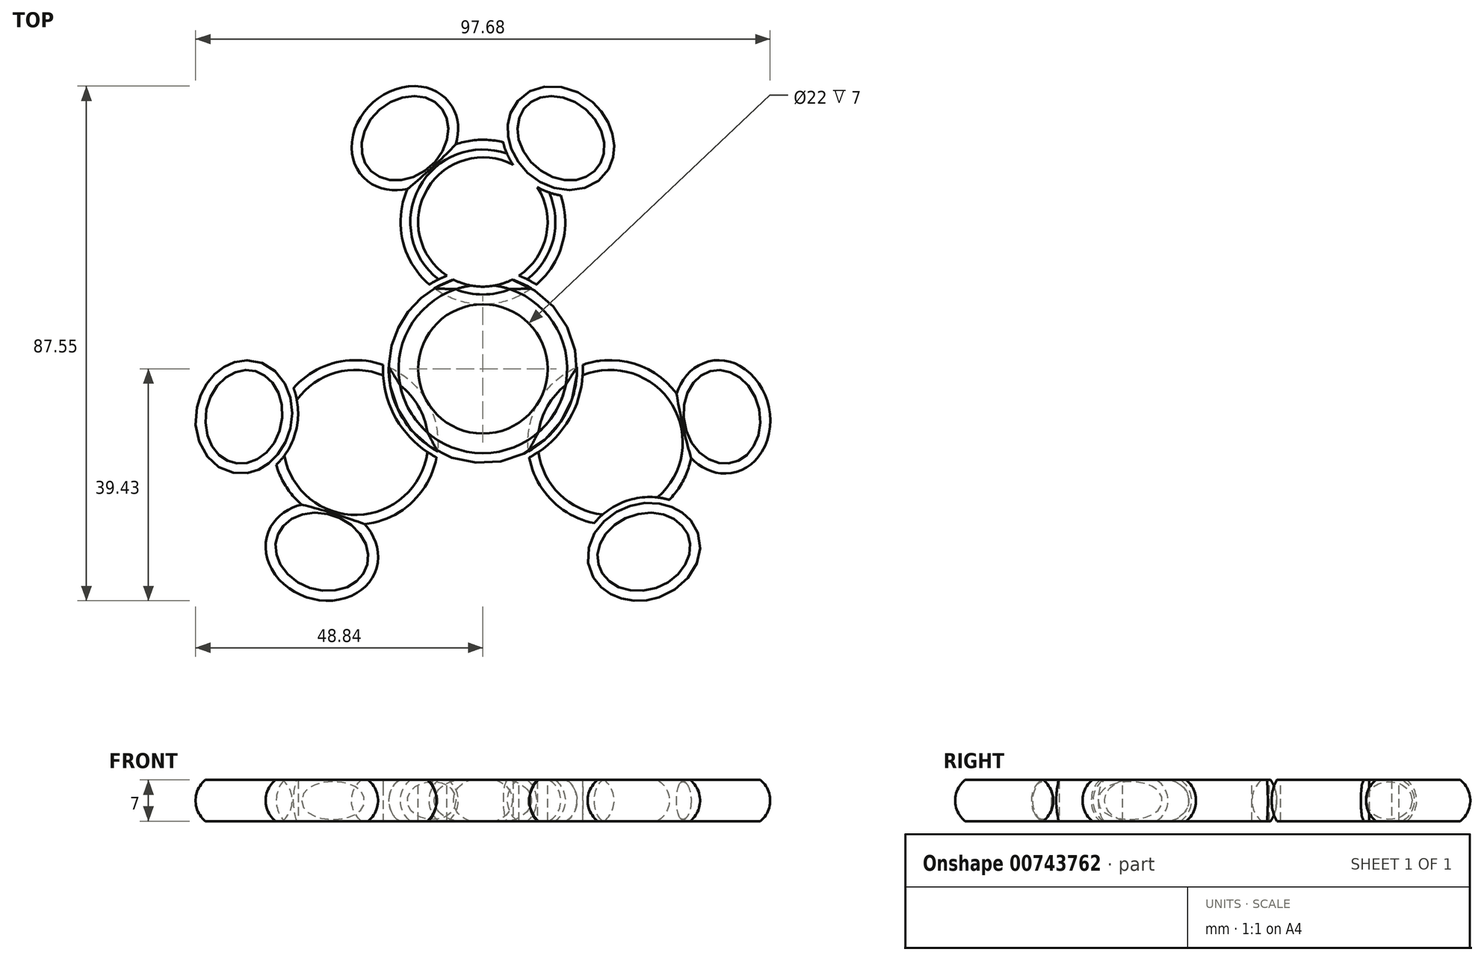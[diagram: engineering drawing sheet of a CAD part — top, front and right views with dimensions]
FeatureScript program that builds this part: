
annotation { "Feature Type Name" : "Feature", "Feature Type Description" : "" }
export const myFeature = defineFeature(function(context is Context, id is Id, definition is map)
    precondition{}
    {
        {
            var Q0;
            Q0=qCreatedBy(makeId("Front.planeOp"),FACE);
            var sketch = newSketch(context, id + "F0", { "sketchPlane" : qUnion([Q0])});
            skLineSegment(sketch, "E0", {"start": v(0, 15.15) * mm, "end": v(0, -20.96) * mm, "construction": true});
            skSolve(sketch);
        }
        {
            var Q0;
            Q0=qCreatedBy(makeId("Top.planeOp"),FACE);
            var sketch = newSketch(context, id + "F1", { "sketchPlane" : qUnion([Q0])});
            skCircle(sketch, "E1", {"center": v(0, 0) * mm, "radius": 39 * mm});
            skCircle(sketch, "E2", {"center": v(0, 0) * mm, "radius": 25 * mm});
            skCircle(sketch, "E3", {"center": v(0, 25) * mm, "radius": 11 * mm});
            skCircle(sketch, "E4", {"center": v(0, 0) * mm, "radius": 11 * mm});
            skCircle(sketch, "E5", {"center": v(0, -25) * mm, "radius": 11 * mm});
            skSolve(sketch);
        }
        {
            var Q0;
            Q0=qCreatedBy(makeId("Top.planeOp"),FACE);
            var sketch = newSketch(context, id + "F2", { "sketchPlane" : qUnion([Q0])});
            skCircle(sketch, "E6", {"center": v(0, 25) * mm, "radius": 14 * mm});
            skSolve(sketch);
        }
        {
            var Q0;
            Q0=qCreatedBy(makeId("Top.planeOp"),FACE);
            var sketch = newSketch(context, id + "F3", { "sketchPlane" : qUnion([Q0])});
            skEllipse(sketch, "E7.MirrorC", {"center": v(13.26, 39.26) * mm, "majorRadius": 9.7 * mm, "minorRadius": 8.15 * mm, "majorAxis": v(-0.75, 0.66)});
            skLineSegment(sketch, "E8", {"start": v(5.97, 45.67) * mm, "end": v(20.54, 32.85) * mm, "construction": true});
            skSolve(sketch);
        }
        {
            var Q0;
            Q0=qSketchRegion(id+"F2",true);
            extrude(context, id + "F4", {"entities" : qUnion([Q0]), "endBound" : BoundingType.SYMMETRIC, "depth" : 7 * mm, "offsetDistance" : 25 * mm});
        }
        {
            var Q0;
            Q0=qCreatedBy(makeId("Right.planeOp"),FACE);
            var sketch = newSketch(context, id + "F5", { "sketchPlane" : qUnion([Q0])});
            skLineSegment(sketch, "E9", {"start": v(39, 3.5) * mm, "end": v(39, -3.5) * mm, "construction": true});
            skArc(sketch, "E10", {"start": v(37.33, -3.5) * mm, "mid": v(39, 0) * mm, "end": v(37.33, 3.5) * mm});
            skLineSegment(sketch, "E11", {"start": v(37.33, 3.5) * mm, "end": v(40, 3.5) * mm});
            skLineSegment(sketch, "E12", {"start": v(40, 3.5) * mm, "end": v(40, -3.5) * mm});
            skLineSegment(sketch, "E13", {"start": v(40, -3.5) * mm, "end": v(37.33, -3.5) * mm});
            skSolve(sketch);
        }
        {
            var Q0;
            Q0=makeQuery(id+"F5.imprint","IMPRINT",FACE,{"disambiguationData":[TD([[makeQuery(id+"F5.imprint","IMPRINT",EDGE,{"derivedFrom":sQuery(id+"F5.wireOp",EDGE,"E10")}),-1.0]])]});
            var Q1;
            Q1=makeQuery(id+"F4.opExtrude","CAP_EDGE",EDGE,{"disambiguationData":[OSD([sQuery(id+"F2.wireOp",EDGE,"E6")])],"isStart":false});
            sweep(context, id + "F6", {"operationType" : NewBodyOperationType.REMOVE, "profiles" : qUnion([Q0]), "path" : qUnion([Q1])});
        }
        {
            var Q0;
            Q0=qSketchRegion(id+"F3",true);
            var Q1;
            Q1=makeQuery(id+"F4.opExtrude","CAP_FACE",FACE,{"disambiguationData":[OSD([sQuery(id+"F2.wireOp",EDGE,"E6")])],"isStart":false});
            var Q2;
            Q2=makeQuery(id+"F4.opExtrude","CAP_FACE",FACE,{"disambiguationData":[OSD([sQuery(id+"F2.wireOp",EDGE,"E6")])],"isStart":true});
            extrude(context, id + "F7", {"entities" : qUnion([Q0]), "endBound" : BoundingType.UP_TO_SURFACE, "depth" : 25 * mm, "endBoundEntityFace" : qUnion([Q1]), "offsetDistance" : 25 * mm, "hasSecondDirection" : true, "secondDirectionBound" : SecondDirectionBoundingType.UP_TO_SURFACE, "secondDirectionOppositeDirection" : true, "secondDirectionDepth" : 25 * mm, "secondDirectionBoundEntityFace" : qUnion([Q2])});
        }
        {
            var Q0;
            Q0=sQuery(id+"F3.wireOp",EDGE,"E8");
            cPoint(context, id + "F8", {"entities" : qUnion([Q0]), "parameter" : 0.5});
        }
        {
            var Q0;
            Q0=qCreatedBy(id+"F8",VERTEX);
            var Q1;
            Q1=sQuery(id+"F3.wireOp",EDGE,"E8");
            cPlane(context, id + "F9", {"entities" : qUnion([Q0, Q1]), "cplaneType" : CPlaneType.LINE_POINT, "offset" : 25 * mm, "width" : 150 * mm, "height" : 150 * mm});
        }
        {
            var Q0;
            Q0=qCreatedBy(id+"F9.planeOp",FACE);
            var sketch = newSketch(context, id + "F10", { "sketchPlane" : qUnion([Q0])});
            skArc(sketch, "E14", {"start": v(44.71, -3.5) * mm, "mid": v(46.39, 0) * mm, "end": v(44.71, 3.5) * mm});
            skLineSegment(sketch, "E15", {"start": v(46.39, 3.5) * mm, "end": v(46.39, -3.5) * mm, "construction": true});
            skLineSegment(sketch, "E16", {"start": v(44.71, 3.5) * mm, "end": v(47.39, 3.5) * mm});
            skLineSegment(sketch, "E17", {"start": v(47.39, 3.5) * mm, "end": v(47.39, -3.5) * mm});
            skLineSegment(sketch, "E18", {"start": v(47.39, -3.5) * mm, "end": v(44.71, -3.5) * mm});
            skSolve(sketch);
        }
        {
            var Q0;
            Q0=makeQuery(id+"F10.imprint","IMPRINT",FACE,{"disambiguationData":[TD([[makeQuery(id+"F10.imprint","IMPRINT",EDGE,{"derivedFrom":sQuery(id+"F10.wireOp",EDGE,"E14")}),-1.0]])]});
            var Q1;
            Q1=makeQuery(id+"F7.opExtrude","CAP_EDGE",EDGE,{"disambiguationData":[OSD([sQuery(id+"F3.wireOp",EDGE,"E7.MirrorC")])],"isStart":false});
            sweep(context, id + "F11", {"operationType" : NewBodyOperationType.REMOVE, "profiles" : qUnion([Q0]), "path" : qUnion([Q1])});
        }
        {
            var Q0;
            Q0=makeQuery(id+"F7.opExtrude","SWEPT_BODY",BODY,{"disambiguationData":[OSD([sQuery(id+"F3.wireOp",EDGE,"E7.MirrorC")])]});
            var Q1;
            Q1=qCreatedBy(makeId("Right.planeOp"),FACE);
            mirror(context, id + "F12", {"operationType" : NewBodyOperationType.ADD, "entities" : qUnion([Q0]), "mirrorPlane" : qUnion([Q1])});
        }
        {
            var Q0;
            Q0=qCreatedBy(makeId("Top.planeOp"),FACE);
            var sketch = newSketch(context, id + "F13", { "sketchPlane" : qUnion([Q0])});
            skCircle(sketch, "E19", {"center": v(0, 0) * mm, "radius": 16 * mm});
            skSolve(sketch);
        }
        {
            var Q0;
            Q0=qSketchRegion(id+"F13",true);
            var Q1;
            Q1=makeQuery(id+"F4.opExtrude","CAP_FACE",FACE,{"disambiguationData":[OSD([sQuery(id+"F2.wireOp",EDGE,"E6")])],"isStart":false});
            var Q2;
            Q2=makeQuery(id+"F4.opExtrude","CAP_FACE",FACE,{"disambiguationData":[OSD([sQuery(id+"F2.wireOp",EDGE,"E6")])],"isStart":true});
            extrude(context, id + "F14", {"entities" : qUnion([Q0]), "endBound" : BoundingType.UP_TO_SURFACE, "depth" : 25 * mm, "endBoundEntityFace" : qUnion([Q1]), "offsetDistance" : 25 * mm, "hasSecondDirection" : true, "secondDirectionBound" : SecondDirectionBoundingType.UP_TO_SURFACE, "secondDirectionOppositeDirection" : true, "secondDirectionDepth" : 25 * mm, "secondDirectionBoundEntityFace" : qUnion([Q2])});
        }
        {
            var Q0;
            Q0=qCreatedBy(makeId("Right.planeOp"),FACE);
            var sketch = newSketch(context, id + "F15", { "sketchPlane" : qUnion([Q0])});
            skArc(sketch, "E20", {"start": v(14.33, -3.5) * mm, "mid": v(16, 0) * mm, "end": v(14.33, 3.5) * mm});
            skLineSegment(sketch, "E21", {"start": v(16, 3.5) * mm, "end": v(16, -3.5) * mm, "construction": true});
            skLineSegment(sketch, "E22", {"start": v(14.33, 3.5) * mm, "end": v(17, 3.5) * mm});
            skLineSegment(sketch, "E23", {"start": v(14.33, -3.5) * mm, "end": v(17, -3.5) * mm});
            skLineSegment(sketch, "E24", {"start": v(17, -3.5) * mm, "end": v(17, 3.5) * mm});
            skSolve(sketch);
        }
        {
            var Q0;
            Q0=makeQuery(id+"F15.imprint","IMPRINT",FACE,{"disambiguationData":[TD([[makeQuery(id+"F15.imprint","IMPRINT",EDGE,{"derivedFrom":sQuery(id+"F15.wireOp",EDGE,"E20")}),-1.0]])]});
            var Q1;
            Q1=sQuery(id+"F0.wireOp",EDGE,"E0");
            revolve(context, id + "F16", {"operationType" : NewBodyOperationType.REMOVE, "surfaceOperationType" : NewSurfaceOperationType.NEW, "entities" : qUnion([Q0]), "axis" : qUnion([Q1]), "revolveType" : RevolveType.FULL, "oppositeDirection" : true});
        }
        {
            var Q0;
            Q0=makeQuery(id+"F4.opExtrude","SWEPT_BODY",BODY,{"disambiguationData":[OSD([sQuery(id+"F2.wireOp",EDGE,"E6")])]});
            var Q1;
            Q1=sQuery(id+"F0.wireOp",EDGE,"E0");
            circularPattern(context, id + "F17", {"entities" : qUnion([Q0]), "axis" : qUnion([Q1]), "angle" : 360 * degree, "instanceCount" : 3, "equalSpace" : true});
        }
        {
            var Q0;
            Q0=makeQuery(id+"F1.imprint","IMPRINT",FACE,{"disambiguationData":[TD([[makeQuery(id+"F1.imprint","IMPRINT",EDGE,{"derivedFrom":sQuery(id+"F1.wireOp",EDGE,"E4")}),1.0]])]});
            extrude(context, id + "F18", {"entities" : qUnion([Q0]), "operationType" : NewBodyOperationType.REMOVE, "endBound" : BoundingType.THROUGH_ALL, "oppositeDirection" : true, "depth" : 25 * mm, "offsetDistance" : 25 * mm, "hasSecondDirection" : true, "secondDirectionBound" : SecondDirectionBoundingType.THROUGH_ALL, "secondDirectionOppositeDirection" : false, "secondDirectionDepth" : 25 * mm});
        }
        {
            var Q0;
            {var subQ0=sQuery(id+"F1.wireOp",EDGE,"E3");var subQ1=sQuery(id+"F1.wireOp",EDGE,"E2");var subQ2=makeQuery(id+"F1.imprint","INTERSECT",VERTEX,{"disambiguationData":[OD(0.0)],"derivedFrom":[subQ1,subQ0]});Q0=makeQuery(id+"F1.imprint","IMPRINT",FACE,{"disambiguationData":[TD([[makeQuery(id+"F1.imprint","IMPRINT",EDGE,{"disambiguationData":[TD([[subQ2,1.0]])],"derivedFrom":subQ1}),-1.0]])]});}
            var Q1;
            {var subQ0=sQuery(id+"F1.wireOp",EDGE,"E3");var subQ1=sQuery(id+"F1.wireOp",EDGE,"E2");var subQ2=makeQuery(id+"F1.imprint","INTERSECT",VERTEX,{"disambiguationData":[OD(0.0)],"derivedFrom":[subQ1,subQ0]});Q1=makeQuery(id+"F1.imprint","IMPRINT",FACE,{"disambiguationData":[TD([[makeQuery(id+"F1.imprint","IMPRINT",EDGE,{"disambiguationData":[TD([[subQ2,1.0]])],"derivedFrom":subQ1}),1.0]])]});}
            extrude(context, id + "F19", {"entities" : qUnion([Q0, Q1]), "operationType" : NewBodyOperationType.REMOVE, "endBound" : BoundingType.THROUGH_ALL, "oppositeDirection" : true, "depth" : 25 * mm, "offsetDistance" : 25 * mm, "hasSecondDirection" : true, "secondDirectionBound" : SecondDirectionBoundingType.THROUGH_ALL, "secondDirectionOppositeDirection" : false, "secondDirectionDepth" : 25 * mm});
        }
    });
